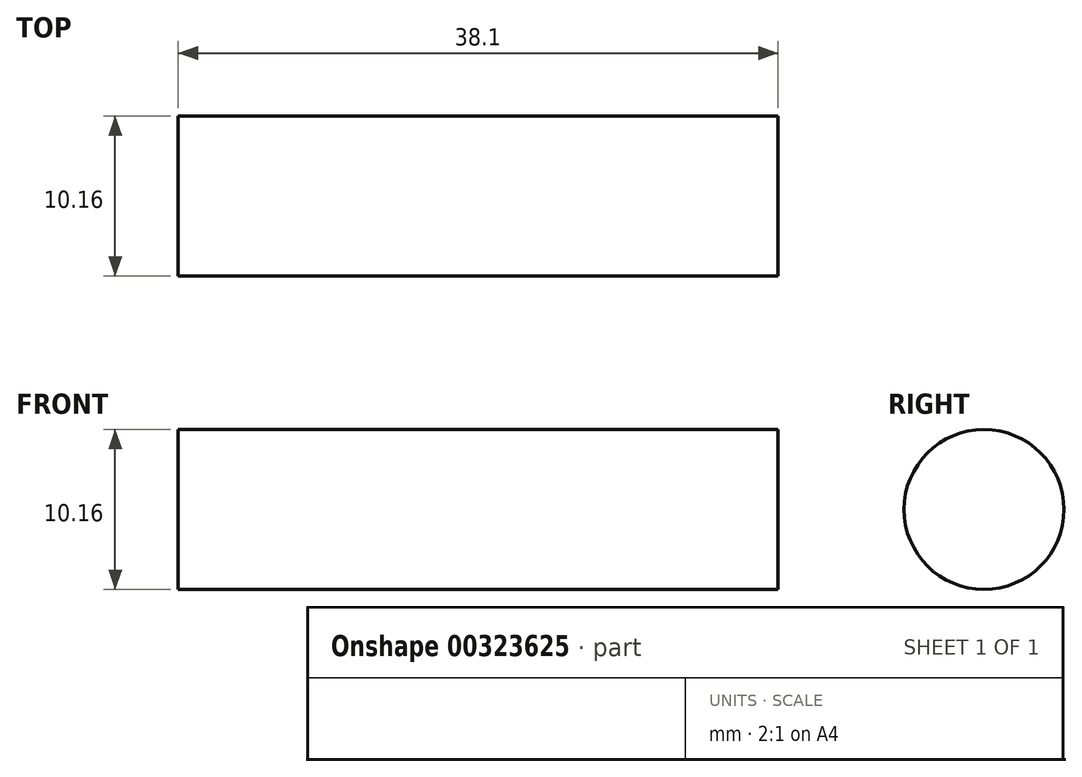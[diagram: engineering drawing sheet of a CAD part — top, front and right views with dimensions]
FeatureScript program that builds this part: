
annotation { "Feature Type Name" : "Feature", "Feature Type Description" : "" }
export const myFeature = defineFeature(function(context is Context, id is Id, definition is map)
    precondition{}
    {
        {
            var Q0;
            Q0=qCreatedBy(makeId("Right.planeOp"),FACE);
            var sketch = newSketch(context, id + "F0", { "sketchPlane" : qUnion([Q0])});
            skCircle(sketch, "E0", {"center": v(0, 0) * mm, "radius": 5.08 * mm});
            skSolve(sketch);
        }
        {
            var Q0;
            Q0=makeQuery(id+"F0.imprint","IMPRINT",FACE,{"disambiguationData":[TD([[makeQuery(id+"F0.imprint","IMPRINT",EDGE,{"derivedFrom":sQuery(id+"F0.wireOp",EDGE,"E0")}),1.0]])]});
            extrude(context, id + "F1", {"entities" : qUnion([Q0]), "depth" : 38.1 * mm});
        }
    });
